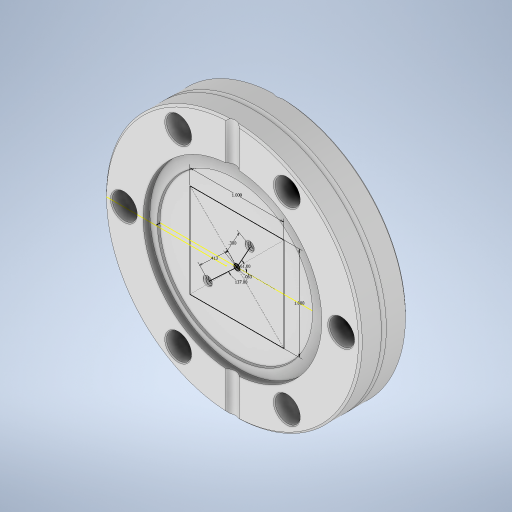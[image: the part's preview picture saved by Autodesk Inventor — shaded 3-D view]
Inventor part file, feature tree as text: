
AUTODESK INVENTOR PART (.ipt)
format: ipt  version: 2024 (Build 280153000, 153)  size: 2,534,912 bytes
history: native  units: in
note: dims shown in document units (in); Inventor stores cm internally (conversion verified against a paired STEP export)
features: move_body x7, sketch x4, other x1, boolean_combine x1, hole x1, pattern_circular x1
ambient origin geometry x8: Origin, YZ Plane, XZ Plane, XY Plane, X Axis, Y Axis, Z Axis, Center Point
bodies: Solid1 (feature_tree), Solid2 (feature_tree), Solid3 (feature_tree)
feature tree (15):
  move_body  "Move Body1"
  move_body  "Move Body2"
  sketch  "Sketch2"  dims[d6=0.0in d7=0.0in d8=-0.1in d9=1.0in d10=0.0in d11=0.0in d12=-1.0in d13=0.0in d14=0.05in]
  sketch  "Sketch3"  dims[d15=1.0in]
  sketch  "Sketch4"  dims[d16=1.0in]
  move_body  "Move Body3"
  move_body  "Move Body4"
  sketch  "Sketch5"  dims[d17=2.5in d18=2.5in d19=0.0in d20=0.0in d21=0.006in d22=0.0in d23=0.0in d24=0.245in d25=0.3001in d26=0.4192in d27=0.4126in d28=0.9414in d29=0.145in d30=0.262in d31=0.0in d32=0.0in d33=0.0in d34=0.251in d35=-0.302in d36=-0.281in d37=0.0in d38=0.0625in d39=0.0625in d40=0.75in d41=0.375in d42=0.25in d43=0.5635in d44=1.0in d45=0.8108in]
  move_body  "Move Body5"
  other  "CirPattern2:1"
  move_body  "Move Body6"
  move_body  "Move Body7"
  boolean_combine  "Combine1"
  hole  "Hole1"  [1 undecoded]
  pattern_circular  "CirPattern2"
note: 1 required parameter value undecoded (feature->parameter linkage not recoverable at this tier; creation-order binding heuristic only, values carry confidence <= 0.55)
